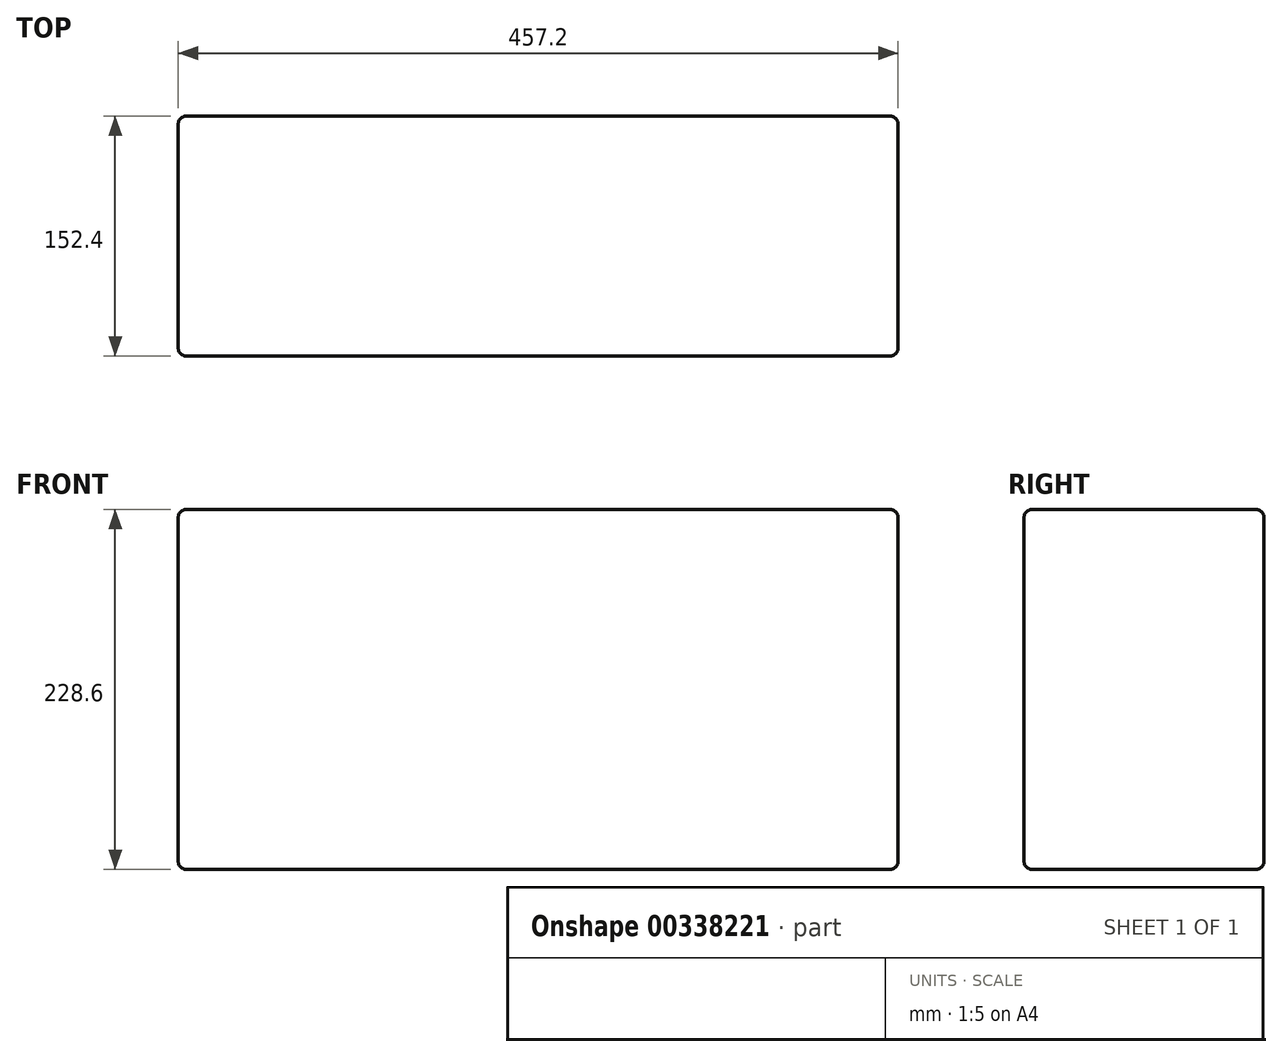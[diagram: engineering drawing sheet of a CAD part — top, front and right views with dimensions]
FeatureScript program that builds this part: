
annotation { "Feature Type Name" : "Feature", "Feature Type Description" : "" }
export const myFeature = defineFeature(function(context is Context, id is Id, definition is map)
    precondition{}
    {
        {
            var Q0;
            Q0=qCreatedBy(makeId("Front.planeOp"),FACE);
            var sketch = newSketch(context, id + "F0", { "sketchPlane" : qUnion([Q0])});
            skLineSegment(sketch, "E0.bottom", {"start": v(258.31, -127.51) * mm, "end": v(-198.89, -127.51) * mm});
            skLineSegment(sketch, "E0.top", {"start": v(258.31, 101.09) * mm, "end": v(-198.89, 101.09) * mm});
            skLineSegment(sketch, "E0.left", {"start": v(258.31, -127.51) * mm, "end": v(258.31, 101.09) * mm});
            skLineSegment(sketch, "E0.right", {"start": v(-198.89, -127.51) * mm, "end": v(-198.89, 101.09) * mm});
            skSolve(sketch);
        }
        {
            var Q0;
            Q0 = qSketchRegion(id + "F0", true);
            extrude(context, id + "F1", {"entities" : qUnion([Q0]), "depth" : 152.4 * mm});
        }
        {
            var Q0;
            Q0=makeQuery(id+"F1.opExtrude","CAP_FACE",FACE,{"disambiguationData":[OSD([sQuery(id+"F0.wireOp",EDGE,"E0.bottom"),sQuery(id+"F0.wireOp",EDGE,"E0.top"),sQuery(id+"F0.wireOp",EDGE,"E0.left"),sQuery(id+"F0.wireOp",EDGE,"E0.right")])],"isStart":false});
            fillet(context, id + "F2", {"entities" : qUnion([Q0]), "radius" : 5.08 * mm, "tangentPropagation" : true, "allowEdgeOverflow" : false});
        }
        {
            var Q0;
            Q0=makeQuery(id+"F1.opExtrude","CAP_FACE",FACE,{"disambiguationData":[OSD([sQuery(id+"F0.wireOp",EDGE,"E0.bottom"),sQuery(id+"F0.wireOp",EDGE,"E0.top"),sQuery(id+"F0.wireOp",EDGE,"E0.left"),sQuery(id+"F0.wireOp",EDGE,"E0.right")])],"isStart":true});
            fillet(context, id + "F3", {"entities" : qUnion([Q0]), "radius" : 5.08 * mm, "tangentPropagation" : true, "allowEdgeOverflow" : false});
        }
        {
            var Q0;
            Q0=makeQuery(id+"F1.opExtrude","SWEPT_FACE",FACE,{"disambiguationData":[OSD([sQuery(id+"F0.wireOp",EDGE,"E0.right")])]});
            var Q1;
            Q1=makeQuery(id+"F1.opExtrude","SWEPT_FACE",FACE,{"disambiguationData":[OSD([sQuery(id+"F0.wireOp",EDGE,"E0.top")])]});
            fillet(context, id + "F4", {"entities" : qUnion([Q0, Q1]), "radius" : 5.08 * mm, "tangentPropagation" : true, "allowEdgeOverflow" : false});
        }
        {
            var Q0;
            Q0=makeQuery(id+"F1.opExtrude","SWEPT_FACE",FACE,{"disambiguationData":[OSD([sQuery(id+"F0.wireOp",EDGE,"E0.left")])]});
            var Q1;
            Q1=makeQuery(id+"F1.opExtrude","SWEPT_FACE",FACE,{"disambiguationData":[OSD([sQuery(id+"F0.wireOp",EDGE,"E0.bottom")])]});
            fillet(context, id + "F5", {"entities" : qUnion([Q0, Q1]), "radius" : 5.08 * mm, "tangentPropagation" : true, "allowEdgeOverflow" : false});
        }
    });
